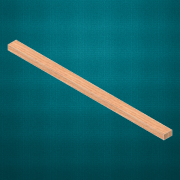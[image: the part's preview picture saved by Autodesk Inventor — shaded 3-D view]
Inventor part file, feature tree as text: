
AUTODESK INVENTOR PART (.ipt)
format: ipt  version: 2017 (Build 210142000, 142)  size: 118,784 bytes
history: native  units: in
note: dims shown in document units (in); Inventor stores cm internally (conversion verified against a paired STEP export)
features: extrude x1, sketch x1
ambient origin geometry x8: Origin, YZ Plane, XZ Plane, XY Plane, X Axis, Y Axis, Z Axis, Center Point
bodies: Solid1 (feature_tree)
feature tree (2):
  extrude  "Extrusion1"  Depth=0.875in
  sketch  "Sketch1"  dims[d0=1.5in d1=0.875in d2=28.25in d3=0.0in]
